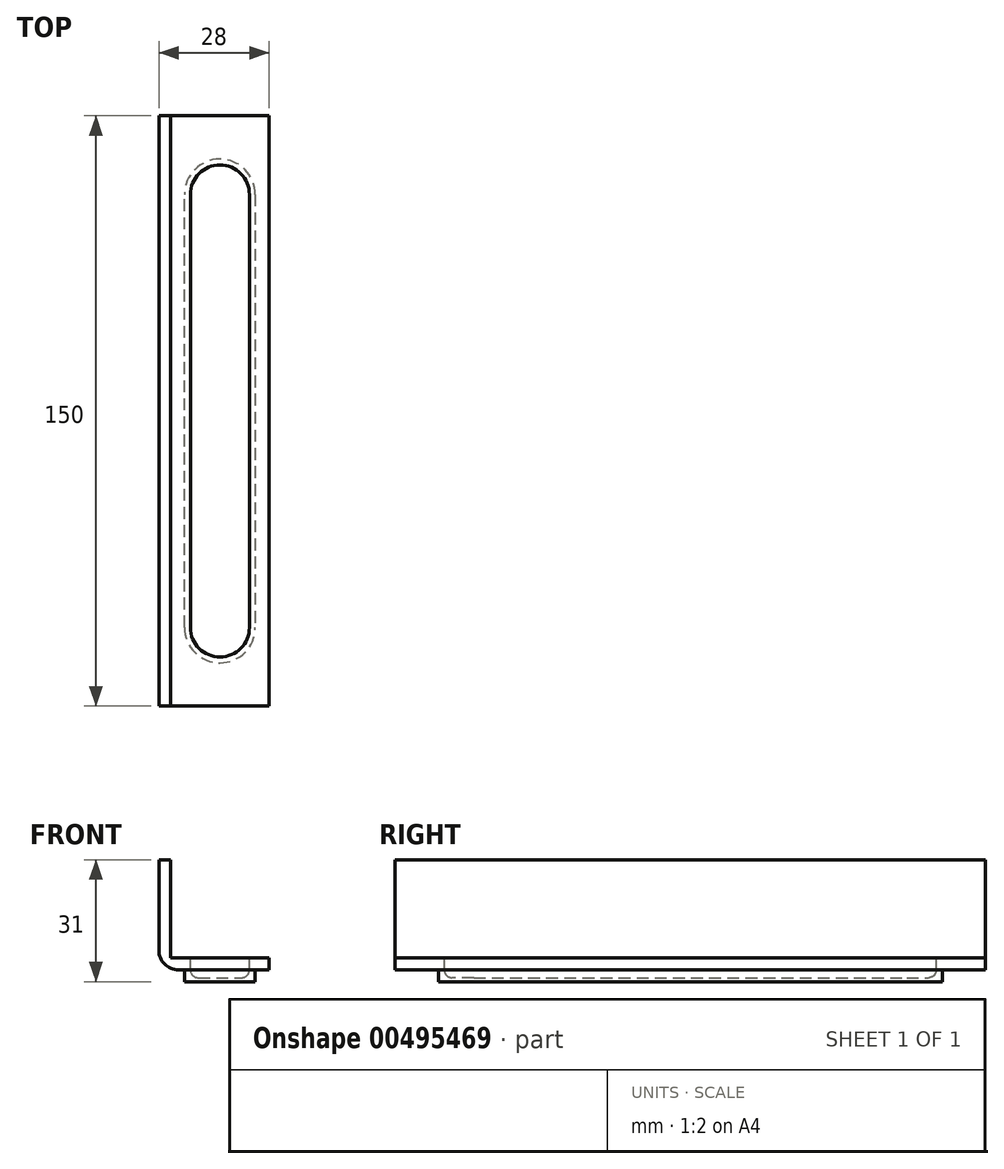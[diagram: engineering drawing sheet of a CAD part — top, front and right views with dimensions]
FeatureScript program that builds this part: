
annotation { "Feature Type Name" : "Feature", "Feature Type Description" : "" }
export const myFeature = defineFeature(function(context is Context, id is Id, definition is map)
    precondition{}
    {
        {
            var Q0;
            Q0=qCreatedBy(makeId("Top.planeOp"),FACE);
            var sketch = newSketch(context, id + "F0", { "sketchPlane" : qUnion([Q0])});
            skLineSegment(sketch, "E0.bottom", {"start": v(0, 0) * mm, "end": v(28, 0) * mm});
            skLineSegment(sketch, "E0.top", {"start": v(0, 150) * mm, "end": v(28, 150) * mm});
            skLineSegment(sketch, "E0.left", {"start": v(0, 0) * mm, "end": v(0, 150) * mm});
            skLineSegment(sketch, "E0.right", {"start": v(28, 0) * mm, "end": v(28, 150) * mm});
            skSolve(sketch);
        }
        {
            var Q0;
            Q0=qSketchRegion(id+"F0",true);
            extrude(context, id + "F1", {"entities" : qUnion([Q0]), "depth" : 3 * mm});
        }
        {
            var Q0;
            Q0=makeQuery(id+"F1.opExtrude","CAP_FACE",FACE,{"disambiguationData":[OSD([sQuery(id+"F0.wireOp",EDGE,"E0.bottom"),sQuery(id+"F0.wireOp",EDGE,"E0.top"),sQuery(id+"F0.wireOp",EDGE,"E0.left"),sQuery(id+"F0.wireOp",EDGE,"E0.right")])],"isStart":false});
            var sketch = newSketch(context, id + "F2", { "sketchPlane" : qUnion([Q0])});
            skCircle(sketch, "E1", {"center": v(15.5, 20) * mm, "radius": 5 * mm});
            skCircle(sketch, "E2", {"center": v(15.5, 130) * mm, "radius": 5 * mm});
            skSolve(sketch);
        }
        {
            var Q0;
            Q0=makeQuery(id+"F1.opExtrude","CAP_FACE",FACE,{"disambiguationData":[OSD([sQuery(id+"F0.wireOp",EDGE,"E0.bottom"),sQuery(id+"F0.wireOp",EDGE,"E0.top"),sQuery(id+"F0.wireOp",EDGE,"E0.left"),sQuery(id+"F0.wireOp",EDGE,"E0.right")])],"isStart":false});
            var sketch = newSketch(context, id + "F3", { "sketchPlane" : qUnion([Q0])});
            skArc(sketch, "E3", {"start": v(24.5, 130) * mm, "mid": v(15.5, 139) * mm, "end": v(6.5, 130) * mm});
            skArc(sketch, "E4", {"start": v(6.5, 20) * mm, "mid": v(15.5, 11) * mm, "end": v(24.5, 20) * mm});
            skLineSegment(sketch, "E5", {"start": v(24.5, 130) * mm, "end": v(24.5, 20) * mm});
            skLineSegment(sketch, "E6", {"start": v(6.5, 20) * mm, "end": v(6.5, 130) * mm});
            skArc(sketch, "E7", {"start": v(8, 20) * mm, "mid": v(15.5, 12.5) * mm, "end": v(23, 20) * mm});
            skArc(sketch, "E8", {"start": v(23, 130) * mm, "mid": v(15.5, 137.5) * mm, "end": v(8, 130) * mm});
            skLineSegment(sketch, "E9", {"start": v(8, 20) * mm, "end": v(8, 130) * mm});
            skLineSegment(sketch, "E10", {"start": v(23, 130) * mm, "end": v(23, 20) * mm});
            skSolve(sketch);
        }
        {
            var Q0;
            Q0=makeQuery(id+"F3.imprint","IMPRINT",FACE,{"disambiguationData":[TD([[makeQuery(id+"F3.imprint","IMPRINT",EDGE,{"derivedFrom":sQuery(id+"F3.wireOp",EDGE,"E3")}),1.0]])]});
            var Q1;
            Q1=makeQuery(id+"F3.imprint","IMPRINT",FACE,{"disambiguationData":[TD([[makeQuery(id+"F3.imprint","IMPRINT",EDGE,{"derivedFrom":sQuery(id+"F3.wireOp",EDGE,"E7")}),1.0]])]});
            extrude(context, id + "F4", {"entities" : qUnion([Q0, Q1]), "operationType" : NewBodyOperationType.ADD, "oppositeDirection" : true, "depth" : 6 * mm});
        }
        {
            var Q0;
            Q0=makeQuery(id+"F3.imprint","IMPRINT",FACE,{"disambiguationData":[TD([[makeQuery(id+"F3.imprint","IMPRINT",EDGE,{"derivedFrom":sQuery(id+"F3.wireOp",EDGE,"E7")}),1.0]])]});
            extrude(context, id + "F5", {"entities" : qUnion([Q0]), "operationType" : NewBodyOperationType.REMOVE, "oppositeDirection" : true, "depth" : 5 * mm});
        }
        {
            var Q0;
            Q0=makeQuery(id+"F5.boolean.opBoolean","COPY",EDGE,{"derivedFrom":makeQuery(id+"F5.opExtrude","CAP_EDGE",EDGE,{"disambiguationData":[OSD([sQuery(id+"F3.wireOp",EDGE,"E9")])],"isStart":true})});
            var Q1;
            Q1=makeQuery(id+"F5.boolean.opBoolean","COPY",EDGE,{"derivedFrom":makeQuery(id+"F5.opExtrude","CAP_EDGE",EDGE,{"disambiguationData":[OSD([sQuery(id+"F3.wireOp",EDGE,"E9")])],"isStart":false})});
            fillet(context, id + "F6", {"entities" : qUnion([Q0, Q1]), "radius" : 2 * mm, "tangentPropagation" : true, "allowEdgeOverflow" : false});
        }
        {
            var Q0;
            Q0=makeQuery(id+"F1.opExtrude","CAP_FACE",FACE,{"disambiguationData":[OSD([sQuery(id+"F0.wireOp",EDGE,"E0.bottom"),sQuery(id+"F0.wireOp",EDGE,"E0.top"),sQuery(id+"F0.wireOp",EDGE,"E0.left"),sQuery(id+"F0.wireOp",EDGE,"E0.right")])],"isStart":false});
            var sketch = newSketch(context, id + "F7", { "sketchPlane" : qUnion([Q0])});
            skLineSegment(sketch, "E11.bottom", {"start": v(0, 150) * mm, "end": v(3, 150) * mm});
            skLineSegment(sketch, "E11.top", {"start": v(0, 0) * mm, "end": v(3, 0) * mm});
            skLineSegment(sketch, "E11.left", {"start": v(0, 150) * mm, "end": v(0, 0) * mm});
            skLineSegment(sketch, "E11.right", {"start": v(3, 150) * mm, "end": v(3, 0) * mm});
            skSolve(sketch);
        }
        {
            var Q0;
            Q0 = qSketchRegion(id + "F7", true);
            extrude(context, id + "F8", {"entities" : qUnion([Q0]), "operationType" : NewBodyOperationType.ADD, "depth" : 25 * mm});
        }
        {
            var Q0;
            Q0=makeQuery(id+"F8.opExtrude","CAP_EDGE",EDGE,{"disambiguationData":[OSD([sQuery(id+"F7.wireOp",EDGE,"E11.right")])],"isStart":true});
            var Q1;
            Q1=makeQuery(id+"F1.opExtrude","CAP_EDGE",EDGE,{"disambiguationData":[OSD([sQuery(id+"F0.wireOp",EDGE,"E0.left")])],"isStart":true});
            fillet(context, id + "F9", {"entities" : qUnion([Q0, Q1]), "radius" : 5 * mm, "tangentPropagation" : true, "allowEdgeOverflow" : false});
        }
    });
